# Revit family: Faucet_Touchless-Lavatory-KOHLER-FASHION-K-13466T_1
name_source: partatom
category: Plumbing Fixtures
revit_build: Autodesk Revit 2017 (Build: 20160225_1515(x64)
units: mm (PartAtom-declared; Revit-internal decimal feet)

## family parameters
Cut with Voids When Loaded = No
Host = Face
OmniClass Number = 23.31.11.00
OmniClass Title = Faucets
Part Type = Normal
Room Calculation Point = No
Round Connector Dimension = Use Diameter
Shared = No

## types (2) — shared parameters
ADA Compliant = No
Assembly Code = D2010
CW Connection = Yes
Cold Water Inlet = Cold Water Inlet
Date Modified = 6/17/2020
Default Elevation = 36"
Description = Fashionable induction faucet direct current (hot and cold mixed type)
Drain Included = No
Flow Rate = 0 GPM
HW Connection = Yes
Height = 5 7/16"
Hot Water Inlet = Hot Water Inlet
Length = 5 5/16"
Manufacturer = KOHLER Co.
Master Format 2014 = 22.41.39
Master Format 2014 Name = Residential Faucets, Supplies, and Trim
Material = Premium Metal Construction
Pressure = 0.00 psi
Product Documentation Link = https://files.kohler.com.cn
Product Name = MODERN
Product Page URL = http://www.kohler.com.cn
Spout Reach = 5 5/16"
Vent Connection = No
Waste Connection = No
Waste Water Outlet = Waste Water Outlet
WaterSense Certified = No
Width = 2 7/16"

## per-type parameters (varying)
| type | Finish | Model | Type | URL |
| CP-Polished Chrome | Kohler-Metal-CP-Polished_Chrome | K-13466T-CP | 1 | http://www.kohler.com.cn |
| AF-Flange Gold | Kohler-Metal-AF-Flange_Gold | K-13466T-AF | 2 | https://www.us.kohler.com |

## geometry (parser evidence)
native form markers: Sweep x4
no freeform markers — native parametric forms only
